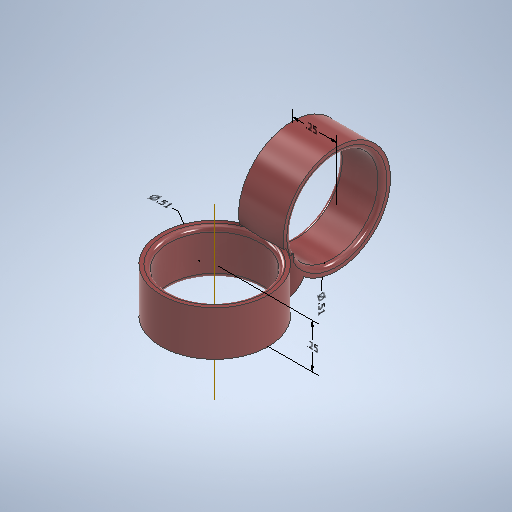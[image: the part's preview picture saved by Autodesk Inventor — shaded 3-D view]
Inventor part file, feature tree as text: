
AUTODESK INVENTOR PART (.ipt)
format: ipt  version: 2025.2 (Build 292293000, 293)  size: 375,808 bytes
history: native  units: in
note: dims shown in document units (in); Inventor stores cm internally (conversion verified against a paired STEP export)
features: other x6, sketch x5, extrude x4, plane x3, fillet x3
ambient origin geometry x8: Origin, YZ Plane, XZ Plane, XY Plane, X Axis, Y Axis, Z Axis, Center Point
bodies: Solid1 (feature_tree)
feature tree (21):
  other  "Annotations"
  extrude  "Extrusion1"  Depth=0.6in
  sketch  "Sketch5"  dims[d4=0.25in d5=0.0in d7=0.6in]
  plane  "Work Plane4"
  plane  "Work Plane5"
  extrude  "Extrusion2"  Depth=0.6in
  extrude  "Extrusion3"  Depth=0.3in
  fillet  "Fillet1"  Radius=0.3in
  fillet  "Fillet3"  Radius=0.3in
  fillet  "Fillet4"  [1 undecoded]
  extrude  "Extrusion5"  Depth=0.6in
  sketch  "Sketch2"  dims[d2=0.51in d3=0.6in]
  plane  "Work Plane3"
  other  "Work Axis1"
  sketch  "Sketch8"  dims[d8=0.6in d9=0.3in d10=0.3in d11=0.3in d12=90.0deg]
  sketch  "Sketch10"  dims[d13=0.51in d14=0.6in]
  sketch  "Sketch13"  dims[d15=0.3in d16=0.25in d17=0.0in d18=0.074in d19=0.0in d20=0.037in d21=0.0in d22=0.125in d26=0.025in d27=0.025in d28=0.0in d29=0.08in d30=0.0in d31=-1.0215in d32=0.1254in d33=0.3566in d34=0.51in d37=0.0695in d38=0.51in d39=0.25in d40=0.25in]
  other  "Diameter Dimension 1"
  other  "Diameter Dimension 2"
  other  "Linear Dimension 1"
  other  "Linear Dimension 2"
note: 1 required parameter value undecoded (feature->parameter linkage not recoverable at this tier; creation-order binding heuristic only, values carry confidence <= 0.55)
